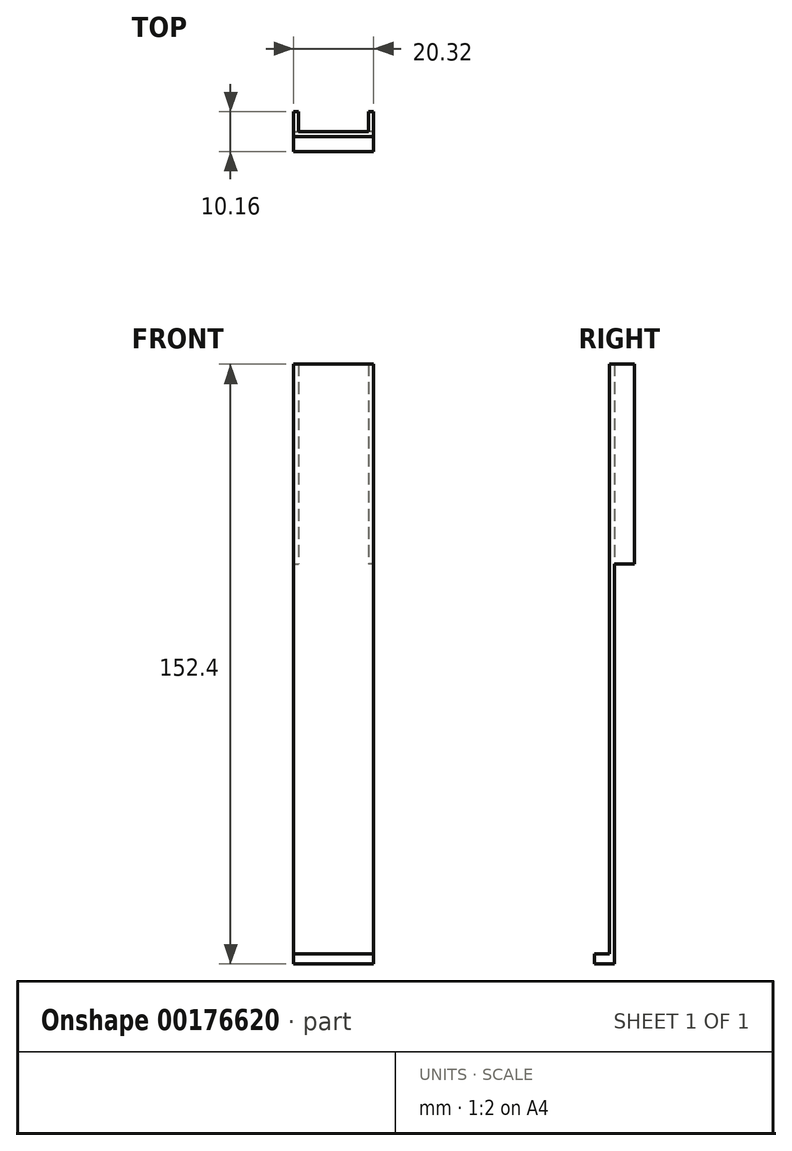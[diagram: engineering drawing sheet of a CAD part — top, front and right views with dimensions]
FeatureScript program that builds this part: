
annotation { "Feature Type Name" : "Feature", "Feature Type Description" : "" }
export const myFeature = defineFeature(function(context is Context, id is Id, definition is map)
    precondition{}
    {
        {
            var Q0;
            Q0=qCreatedBy(makeId("Front.planeOp"),FACE);
            var sketch = newSketch(context, id + "F0", { "sketchPlane" : qUnion([Q0])});
            skLineSegment(sketch, "E0.bottom", {"start": v(0, 0) * mm, "end": v(20.32, 0) * mm});
            skLineSegment(sketch, "E0.top", {"start": v(0, 152.4) * mm, "end": v(20.32, 152.4) * mm});
            skLineSegment(sketch, "E0.left", {"start": v(0, 0) * mm, "end": v(0, 152.4) * mm});
            skLineSegment(sketch, "E0.right", {"start": v(20.32, 0) * mm, "end": v(20.32, 152.4) * mm});
            skSolve(sketch);
        }
        {
            var Q0;
            Q0=makeQuery(id+"F0.imprint","IMPRINT",FACE,{"disambiguationData":[TD([[makeQuery(id+"F0.imprint","IMPRINT",EDGE,{"derivedFrom":sQuery(id+"F0.wireOp",EDGE,"E0.bottom")}),1.0]])]});
            extrude(context, id + "F1", {"entities" : qUnion([Q0]), "depth" : 1.27 * mm});
        }
        {
            var Q0;
            Q0=makeQuery(id+"F1.opExtrude","CAP_FACE",FACE,{"disambiguationData":[OSD([sQuery(id+"F0.wireOp",EDGE,"E0.bottom"),sQuery(id+"F0.wireOp",EDGE,"E0.top"),sQuery(id+"F0.wireOp",EDGE,"E0.left"),sQuery(id+"F0.wireOp",EDGE,"E0.right")])],"isStart":false});
            var sketch = newSketch(context, id + "F2", { "sketchPlane" : qUnion([Q0])});
            skLineSegment(sketch, "E1.bottom", {"start": v(0, 0) * mm, "end": v(20.32, 0) * mm});
            skLineSegment(sketch, "E1.top", {"start": v(0, 2.54) * mm, "end": v(20.32, 2.54) * mm});
            skLineSegment(sketch, "E1.left", {"start": v(0, 0) * mm, "end": v(0, 2.54) * mm});
            skLineSegment(sketch, "E1.right", {"start": v(20.32, 0) * mm, "end": v(20.32, 2.54) * mm});
            skSolve(sketch);
        }
        {
            var Q0;
            Q0=makeQuery(id+"F2.imprint","IMPRINT",FACE,{"disambiguationData":[TD([[makeQuery(id+"F2.imprint","IMPRINT",EDGE,{"derivedFrom":sQuery(id+"F2.wireOp",EDGE,"E1.bottom")}),1.0]])]});
            extrude(context, id + "F3", {"entities" : qUnion([Q0]), "operationType" : NewBodyOperationType.ADD, "depth" : 3.8 * mm});
        }
        {
            var Q0;
            Q0=makeQuery(id+"F1.opExtrude","CAP_FACE",FACE,{"disambiguationData":[OSD([sQuery(id+"F0.wireOp",EDGE,"E0.bottom"),sQuery(id+"F0.wireOp",EDGE,"E0.top"),sQuery(id+"F0.wireOp",EDGE,"E0.left"),sQuery(id+"F0.wireOp",EDGE,"E0.right")])],"isStart":true});
            var sketch = newSketch(context, id + "F4", { "sketchPlane" : qUnion([Q0])});
            skLineSegment(sketch, "E2.bottom", {"start": v(-20.32, 152.4) * mm, "end": v(-19.05, 152.4) * mm});
            skLineSegment(sketch, "E2.top", {"start": v(-20.32, 101.6) * mm, "end": v(-19.05, 101.6) * mm});
            skLineSegment(sketch, "E2.left", {"start": v(-20.32, 152.4) * mm, "end": v(-20.32, 101.6) * mm});
            skLineSegment(sketch, "E2.right", {"start": v(-19.05, 152.4) * mm, "end": v(-19.05, 101.6) * mm});
            skLineSegment(sketch, "E3.bottom", {"start": v(0, 152.4) * mm, "end": v(-1.27, 152.4) * mm});
            skLineSegment(sketch, "E3.top", {"start": v(0, 101.6) * mm, "end": v(-1.27, 101.6) * mm});
            skLineSegment(sketch, "E3.left", {"start": v(0, 152.4) * mm, "end": v(0, 101.6) * mm});
            skLineSegment(sketch, "E3.right", {"start": v(-1.27, 152.4) * mm, "end": v(-1.27, 101.6) * mm});
            skSolve(sketch);
        }
        {
            var Q0;
            Q0=makeQuery(id+"F4.imprint","IMPRINT",FACE,{"disambiguationData":[TD([[makeQuery(id+"F4.imprint","IMPRINT",EDGE,{"derivedFrom":sQuery(id+"F4.wireOp",EDGE,"E3.bottom")}),1.0]])]});
            var Q1;
            Q1=makeQuery(id+"F4.imprint","IMPRINT",FACE,{"disambiguationData":[TD([[makeQuery(id+"F4.imprint","IMPRINT",EDGE,{"derivedFrom":sQuery(id+"F4.wireOp",EDGE,"E2.bottom")}),1.0]])]});
            extrude(context, id + "F5", {"entities" : qUnion([Q0, Q1]), "operationType" : NewBodyOperationType.ADD, "depth" : 5.08 * mm});
        }
    });
